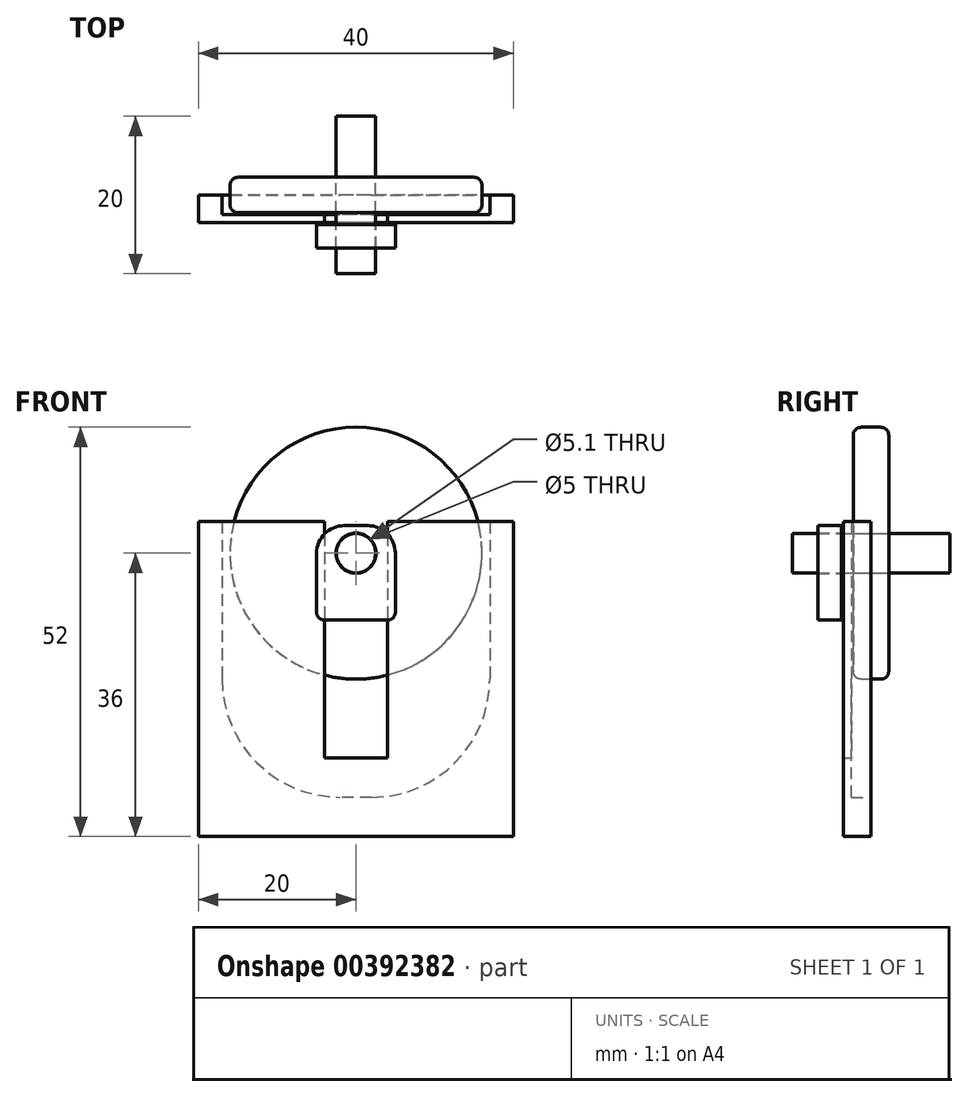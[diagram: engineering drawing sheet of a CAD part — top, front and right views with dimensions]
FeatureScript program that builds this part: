
annotation { "Feature Type Name" : "Feature", "Feature Type Description" : "" }
export const myFeature = defineFeature(function(context is Context, id is Id, definition is map)
    precondition{}
    {
        {
            var Q0;
            Q0=qCreatedBy(makeId("Front.planeOp"),FACE);
            var sketch = newSketch(context, id + "F0", { "sketchPlane" : qUnion([Q0])});
            skCircle(sketch, "E0", {"center": v(0, 0) * mm, "radius": 2.5 * mm});
            skCircle(sketch, "E1", {"center": v(0, 0) * mm, "radius": 16 * mm});
            skSolve(sketch);
        }
        {
            var Q0;
            Q0 = qSketchRegion(id + "F0", true);
            extrude(context, id + "F1", {"entities" : qUnion([Q0]), "endBound" : BoundingType.SYMMETRIC, "depth" : 4.5 * mm});
        }
        {
            var Q0;
            Q0=qCreatedBy(makeId("Front.planeOp"),FACE);
            var sketch = newSketch(context, id + "F2", { "sketchPlane" : qUnion([Q0])});
            skCircle(sketch, "E2", {"center": v(0, 0) * mm, "radius": 2.5 * mm});
            skSolve(sketch);
        }
        {
            var Q0;
            Q0 = qSketchRegion(id + "F2", true);
            extrude(context, id + "F3", {"entities" : qUnion([Q0]), "endBound" : BoundingType.SYMMETRIC, "depth" : 20 * mm});
        }
        {
            var Q0;
            Q0=makeQuery(id+"F1.opExtrude","CAP_FACE",FACE,{"disambiguationData":[OSD([sQuery(id+"F0.wireOp",EDGE,"E0"),sQuery(id+"F0.wireOp",EDGE,"E1")])],"isStart":false});
            cPlane(context, id + "F4", {"entities" : qUnion([Q0]), "cplaneType" : CPlaneType.OFFSET, "offset" : 1.5 * mm, "width" : 150 * mm, "height" : 150 * mm});
        }
        {
            var Q0;
            Q0=qCreatedBy(id+"F4.planeOp",FACE);
            var sketch = newSketch(context, id + "F5", { "sketchPlane" : qUnion([Q0])});
            skLineSegment(sketch, "E3.bottom", {"start": v(5, 3.5) * mm, "end": v(-5, 3.5) * mm});
            skLineSegment(sketch, "E3.top", {"start": v(5, -8.5) * mm, "end": v(-5, -8.5) * mm});
            skLineSegment(sketch, "E3.left", {"start": v(5, 3.5) * mm, "end": v(5, -8.5) * mm});
            skLineSegment(sketch, "E3.right", {"start": v(-5, 3.5) * mm, "end": v(-5, -8.5) * mm});
            skPoint(sketch, "E3.middle", {"position": v(0, -2.5) * mm});
            skCircle(sketch, "E4", {"center": v(0, 0) * mm, "radius": 2.55 * mm});
            skSolve(sketch);
        }
        {
            var Q0;
            Q0 = qSketchRegion(id + "F5", true);
            extrude(context, id + "F6", {"entities" : qUnion([Q0]), "depth" : 3 * mm});
        }
        {
            var Q0;
            Q0=makeQuery(id+"F6.opExtrude","SWEPT_EDGE",EDGE,{"disambiguationData":[OSD([sQuery(id+"F5.wireOp",EDGE,"E3.bottom"),sQuery(id+"F5.wireOp",EDGE,"E3.right")])]});
            var Q1;
            Q1=makeQuery(id+"F6.opExtrude","SWEPT_EDGE",EDGE,{"disambiguationData":[OSD([sQuery(id+"F5.wireOp",EDGE,"E3.bottom"),sQuery(id+"F5.wireOp",EDGE,"E3.left")])]});
            fillet(context, id + "F7", {"entities" : qUnion([Q0, Q1]), "radius" : 3.5 * mm, "tangentPropagation" : true, "allowEdgeOverflow" : false});
        }
        {
            var Q0;
            Q0=makeQuery(id+"F1.opExtrude","CAP_EDGE",EDGE,{"disambiguationData":[OSD([sQuery(id+"F0.wireOp",EDGE,"E1")])],"isStart":false});
            var Q1;
            Q1=makeQuery(id+"F1.opExtrude","CAP_EDGE",EDGE,{"disambiguationData":[OSD([sQuery(id+"F0.wireOp",EDGE,"E1")])],"isStart":true});
            var Q2;
            Q2=makeQuery(id+"F6.opExtrude","SWEPT_EDGE",EDGE,{"disambiguationData":[OSD([sQuery(id+"F5.wireOp",EDGE,"E3.top"),sQuery(id+"F5.wireOp",EDGE,"E3.left")])]});
            var Q3;
            Q3=makeQuery(id+"F6.opExtrude","SWEPT_EDGE",EDGE,{"disambiguationData":[OSD([sQuery(id+"F5.wireOp",EDGE,"E3.top"),sQuery(id+"F5.wireOp",EDGE,"E3.right")])]});
            fillet(context, id + "F8", {"entities" : qUnion([Q0, Q1, Q2, Q3]), "radius" : 1 * mm, "tangentPropagation" : true, "allowEdgeOverflow" : false});
        }
        {
            var Q0;
            Q0=qCreatedBy(makeId("Front.planeOp"),FACE);
            var sketch = newSketch(context, id + "F9", { "sketchPlane" : qUnion([Q0])});
            skLineSegment(sketch, "E5.bottom", {"start": v(20, 4) * mm, "end": v(-20, 4) * mm});
            skLineSegment(sketch, "E5.top", {"start": v(20, -36) * mm, "end": v(-20, -36) * mm});
            skLineSegment(sketch, "E5.left", {"start": v(20, 4) * mm, "end": v(20, -36) * mm});
            skLineSegment(sketch, "E5.right", {"start": v(-20, 4) * mm, "end": v(-20, -36) * mm});
            skPoint(sketch, "E5.middle", {"position": v(0, -16) * mm});
            skLineSegment(sketch, "E6.bottom", {"start": v(17, 4) * mm, "end": v(-17, 4) * mm});
            skLineSegment(sketch, "E6.top", {"start": v(2, -31) * mm, "end": v(-2, -31) * mm});
            skLineSegment(sketch, "E6.left", {"start": v(17, 4) * mm, "end": v(17, -16) * mm});
            skLineSegment(sketch, "E6.right", {"start": v(-17, 4) * mm, "end": v(-17, -16) * mm});
            skPoint(sketch, "E6.middle", {"position": v(0, -13.5) * mm});
            skPoint(sketch, "E7.visualSharp", {"position": v(-17, -31) * mm});
            skArc(sketch, "E7.filletArc", {"start": v(-17, -16) * mm, "mid": v(-12.6, -26.6) * mm, "end": v(-2, -31) * mm});
            skPoint(sketch, "E8.visualSharp", {"position": v(17, -31) * mm});
            skArc(sketch, "E8.filletArc", {"start": v(2, -31) * mm, "mid": v(12.6, -26.6) * mm, "end": v(17, -16) * mm});
            skSolve(sketch);
        }
        {
            var Q0;
            Q0=makeQuery(id+"F9.imprint","IMPRINT",FACE,{"disambiguationData":[TD([[makeQuery(id+"F9.imprint","IMPRINT",EDGE,{"derivedFrom":sQuery(id+"F9.wireOp",EDGE,"E5.top")}),-1.0]])]});
            extrude(context, id + "F10", {"entities" : qUnion([Q0]), "depth" : 2.5 * mm});
        }
        {
            var Q0;
            Q0=makeQuery(id+"F10.opExtrude","CAP_FACE",FACE,{"disambiguationData":[OSD([sQuery(id+"F9.wireOp",EDGE,"E5.bottom"),sQuery(id+"F9.wireOp",EDGE,"E5.top"),sQuery(id+"F9.wireOp",EDGE,"E5.left"),sQuery(id+"F9.wireOp",EDGE,"E5.right"),sQuery(id+"F9.wireOp",EDGE,"E6.top"),sQuery(id+"F9.wireOp",EDGE,"E6.left"),sQuery(id+"F9.wireOp",EDGE,"E6.right"),sQuery(id+"F9.wireOp",EDGE,"E7.filletArc"),sQuery(id+"F9.wireOp",EDGE,"E8.filletArc")])],"isStart":false});
            var sketch = newSketch(context, id + "F11", { "sketchPlane" : qUnion([Q0])});
            skLineSegment(sketch, "E9.bottom", {"start": v(-20, 4) * mm, "end": v(20, 4) * mm});
            skLineSegment(sketch, "E9.top", {"start": v(-20, -36) * mm, "end": v(20, -36) * mm});
            skLineSegment(sketch, "E9.left", {"start": v(-20, 4) * mm, "end": v(-20, -36) * mm});
            skLineSegment(sketch, "E9.right", {"start": v(20, 4) * mm, "end": v(20, -36) * mm});
            skLineSegment(sketch, "E10.bottom", {"start": v(4, 4) * mm, "end": v(-4, 4) * mm});
            skLineSegment(sketch, "E10.top", {"start": v(4, -26) * mm, "end": v(-4, -26) * mm});
            skLineSegment(sketch, "E10.left", {"start": v(4, 4) * mm, "end": v(4, -26) * mm});
            skLineSegment(sketch, "E10.right", {"start": v(-4, 4) * mm, "end": v(-4, -26) * mm});
            skPoint(sketch, "E10.middle", {"position": v(0, -11) * mm});
            skLineSegment(sketch, "E11.bottom", {"start": v(-4, 4) * mm, "end": v(4, 4) * mm});
            skLineSegment(sketch, "E11.top", {"start": v(-4, 3) * mm, "end": v(4, 3) * mm});
            skLineSegment(sketch, "E11.left", {"start": v(-4, 4) * mm, "end": v(-4, 3) * mm});
            skLineSegment(sketch, "E11.right", {"start": v(4, 4) * mm, "end": v(4, 3) * mm});
            skSolve(sketch);
        }
        {
            var Q0;
            Q0=makeQuery(id+"F11.imprint","IMPRINT",FACE,{"disambiguationData":[TD([[makeQuery(id+"F11.imprint","IMPRINT",EDGE,{"derivedFrom":sQuery(id+"F11.wireOp",EDGE,"E9.top")}),-1.0]])]});
            var Q1;
            Q1=makeQuery(id+"F11.imprint","IMPRINT",FACE,{"disambiguationData":[TD([[makeQuery(id+"F11.imprint","IMPRINT",EDGE,{"derivedFrom":sQuery(id+"F11.wireOp",EDGE,"E10.top")}),1.0]])]});
            var Q2;
            Q2=makeQuery(id+"F11.imprint","IMPRINT",FACE,{"disambiguationData":[TD([[makeQuery(id+"F11.imprint","IMPRINT",EDGE,{"derivedFrom":sQuery(id+"F11.wireOp",EDGE,"E11.bottom")}),-1.0]])]});
            extrude(context, id + "F12", {"entities" : qUnion([Q0, Q1, Q2]), "operationType" : NewBodyOperationType.ADD, "depth" : 1 * mm});
        }
    });
